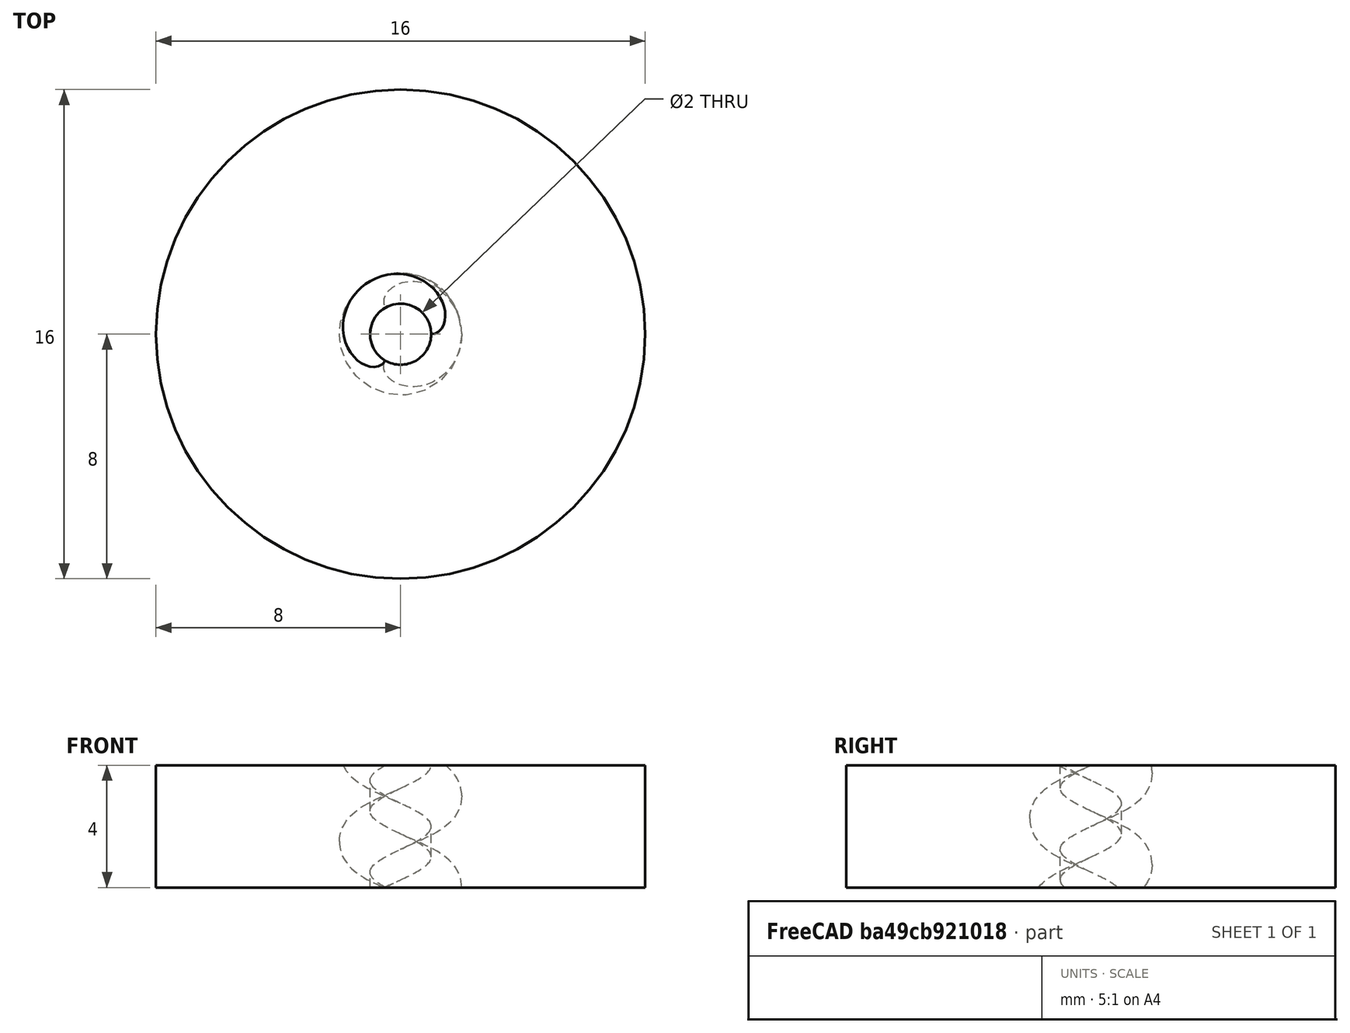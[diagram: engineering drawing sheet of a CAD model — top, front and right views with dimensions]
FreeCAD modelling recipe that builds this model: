
FCSTD DOCUMENT  (FreeCAD 0.16R)
Label: PidFan-Rosca
License: All rights reserved
LicenseURL: http://en.wikipedia.org/wiki/All_rights_reserved
objects: Part::Cylinder×2, Part::Cut×2, Sketcher::SketchObject×1, Part::Helix×1, Part::Sweep×1
note: 7 computed .brp shape members not serialized (recipe doc carries the construction recipe); baked Part::Feature solids carry a one-line shape summary decoded from their .brp

FEATURE [Sketcher::SketchObject] Sketch007  label="Helix Sketch"
  Placement = pos=(1,0,0) rot=(1,0,0;1.5708rad)
  sketch-geometry (1):
    g0: Circle CenterX=0 CenterY=0 CenterZ=0 NormalX=0 NormalY=0 NormalZ=1 Radius=1
  constraints (2):
    c: Coincident(g0,g-1)
    c: Radius(g0) = 1
FEATURE [Part::Helix] Helix004  label="Helix"
  Angle = 0
  Height = 16
  LocalCoord = 0
  Pitch = 3
  Radius = 1
  Style = 1
FEATURE [Part::Sweep] Sweep003  label="Rosca 004"
  Frenet = true
  Placement = pos=(0,0,-6) rot=(0,0,1;0rad)
  Sections = -> [Sketch007]
  Solid = true
  Spine = -> Helix004 [Edge1,Edge2,Edge3,Edge4,Edge5,Edge6]
  Transition = 1
FEATURE [Part::Cylinder] Cylinder
  Angle = 360
  Height = 4
  Radius = 8
FEATURE [Part::Cylinder] Cylinder001
  Angle = 360
  Height = 25
  Placement = pos=(0,0,-10) rot=(0,0,1;0rad)
  Radius = 1
FEATURE [Part::Cut] Cut
  Base = -> Cylinder
  Tool = -> Cylinder001
FEATURE [Part::Cut] Cut001
  Base = -> Cut
  Tool = -> Sweep003
